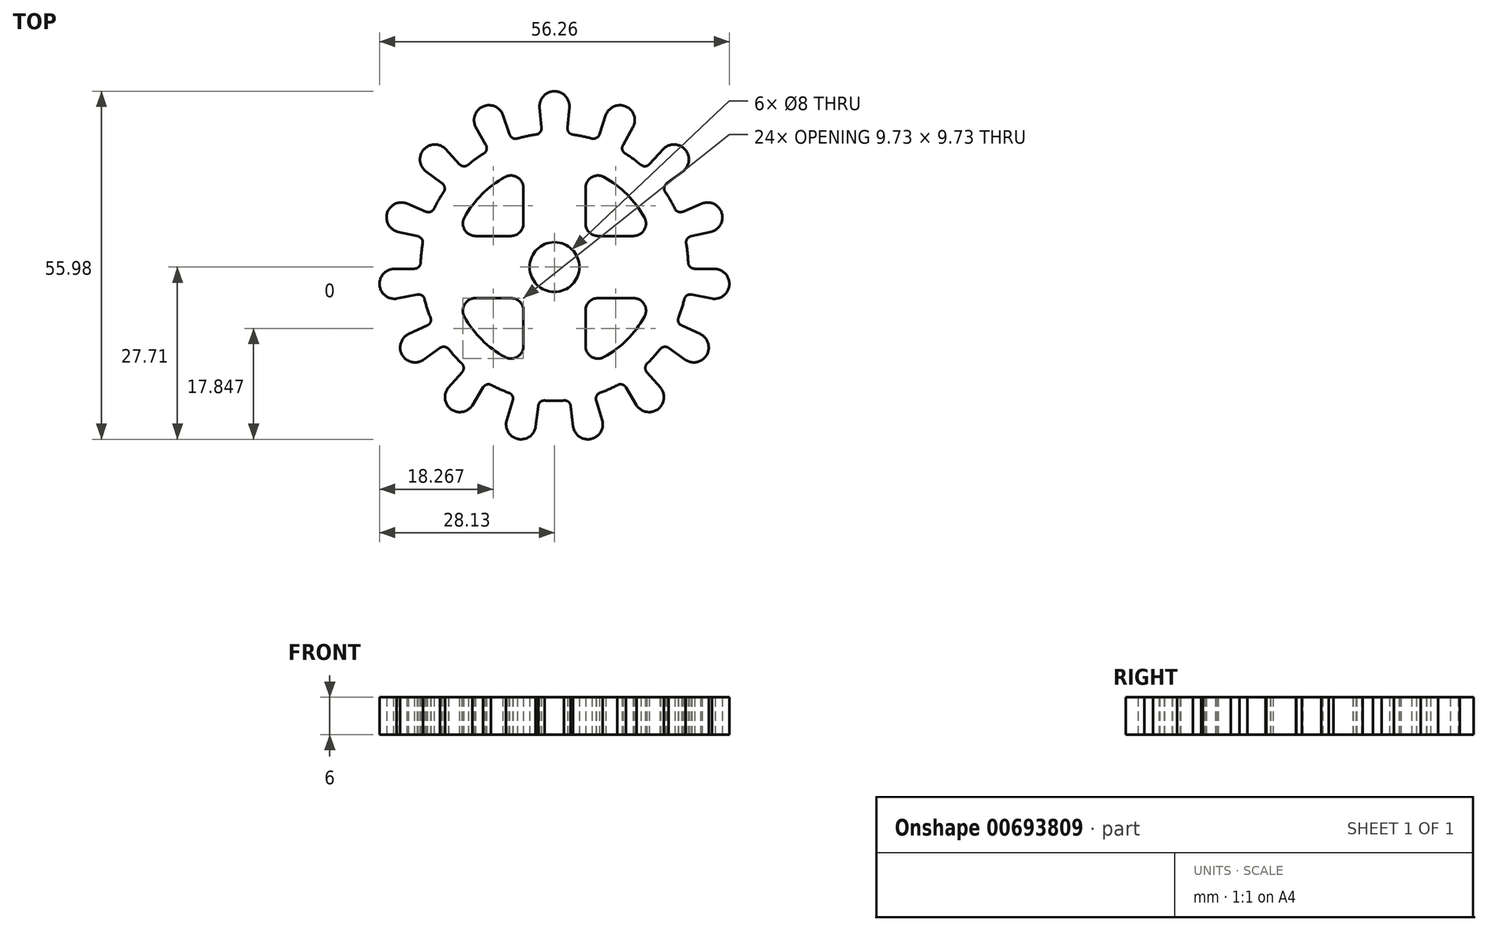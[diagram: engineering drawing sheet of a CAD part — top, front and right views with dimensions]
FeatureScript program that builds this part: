
annotation { "Feature Type Name" : "Feature", "Feature Type Description" : "" }
export const myFeature = defineFeature(function(context is Context, id is Id, definition is map)
    precondition{}
    {
        {
            var Q0;
            Q0=qCreatedBy(makeId("Top.planeOp"),FACE);
            var sketch = newSketch(context, id + "F0", { "sketchPlane" : qUnion([Q0])});
            skCircle(sketch, "E0", {"center": v(0, 0) * mm, "radius": 25.88 * mm, "construction": true});
            skArc(sketch, "E1", {"start": v(-2.4, 25.76) * mm, "mid": v(0, 28.28) * mm, "end": v(2.4, 25.76) * mm});
            skLineSegment(sketch, "E2.anchor1", {"start": v(0, 0) * mm, "end": v(0, 25.88) * mm, "construction": true});
            skLineSegment(sketch, "E3", {"start": v(2.4, 25.76) * mm, "end": v(2.09, 22.43) * mm});
            skLineSegment(sketch, "E4", {"start": v(8.29, 24.51) * mm, "end": v(7.22, 21.34) * mm});
            skArc(sketch, "E5", {"start": v(2.09, 22.43) * mm, "mid": v(2.3, 21.68) * mm, "end": v(2.99, 21.32) * mm});
            skArc(sketch, "E6", {"start": v(6.03, 20.66) * mm, "mid": v(6.75, 20.77) * mm, "end": v(7.22, 21.34) * mm});
            skArc(sketch, "E7", {"start": v(6.03, 20.66) * mm, "mid": v(4.52, 21.05) * mm, "end": v(2.99, 21.32) * mm});
            skLineSegment(sketch, "E8.1.0", {"start": v(12.67, 22.56) * mm, "end": v(11.03, 19.64) * mm});
            skArc(sketch, "E8.1.1", {"start": v(13.91, 16.43) * mm, "mid": v(12.69, 17.39) * mm, "end": v(11.4, 18.26) * mm});
            skArc(sketch, "E8.1.2", {"start": v(8.29, 24.51) * mm, "mid": v(11.5, 25.83) * mm, "end": v(12.67, 22.56) * mm});
            skLineSegment(sketch, "E8.1.3", {"start": v(17.54, 19.02) * mm, "end": v(15.27, 16.56) * mm});
            skArc(sketch, "E8.1.4", {"start": v(13.91, 16.43) * mm, "mid": v(14.62, 16.22) * mm, "end": v(15.27, 16.56) * mm});
            skArc(sketch, "E8.1.5", {"start": v(11.03, 19.64) * mm, "mid": v(10.92, 18.87) * mm, "end": v(11.4, 18.26) * mm});
            skLineSegment(sketch, "E8.2.0", {"start": v(20.75, 15.46) * mm, "end": v(18.06, 13.46) * mm});
            skArc(sketch, "E8.2.1", {"start": v(19.39, 9.35) * mm, "mid": v(18.66, 10.72) * mm, "end": v(17.84, 12.04) * mm});
            skArc(sketch, "E8.2.2", {"start": v(17.54, 19.02) * mm, "mid": v(21.01, 18.92) * mm, "end": v(20.75, 15.46) * mm});
            skLineSegment(sketch, "E8.2.3", {"start": v(23.76, 10.24) * mm, "end": v(20.69, 8.92) * mm});
            skArc(sketch, "E8.2.4", {"start": v(19.39, 9.35) * mm, "mid": v(19.95, 8.88) * mm, "end": v(20.69, 8.92) * mm});
            skArc(sketch, "E8.2.5", {"start": v(18.06, 13.46) * mm, "mid": v(17.65, 12.8) * mm, "end": v(17.84, 12.04) * mm});
            skLineSegment(sketch, "E8.3.0", {"start": v(25.24, 5.68) * mm, "end": v(21.98, 4.95) * mm});
            skArc(sketch, "E8.3.1", {"start": v(21.52, 0.65) * mm, "mid": v(21.41, 2.2) * mm, "end": v(21.2, 3.75) * mm});
            skArc(sketch, "E8.3.2", {"start": v(23.76, 10.24) * mm, "mid": v(26.9, 8.74) * mm, "end": v(25.24, 5.68) * mm});
            skLineSegment(sketch, "E8.3.3", {"start": v(25.87, -0.3) * mm, "end": v(22.52, -0.27) * mm});
            skArc(sketch, "E8.3.4", {"start": v(21.52, 0.65) * mm, "mid": v(21.84, 0) * mm, "end": v(22.52, -0.27) * mm});
            skArc(sketch, "E8.3.5", {"start": v(21.98, 4.95) * mm, "mid": v(21.33, 4.5) * mm, "end": v(21.2, 3.75) * mm});
            skLineSegment(sketch, "E8.4.0", {"start": v(25.37, -5.08) * mm, "end": v(22.09, -4.42) * mm});
            skArc(sketch, "E8.4.1", {"start": v(19.92, -8.15) * mm, "mid": v(20.46, -6.7) * mm, "end": v(20.89, -5.2) * mm});
            skArc(sketch, "E8.4.2", {"start": v(25.87, -0.3) * mm, "mid": v(28.12, -2.96) * mm, "end": v(25.37, -5.08) * mm});
            skLineSegment(sketch, "E8.4.3", {"start": v(23.51, -10.8) * mm, "end": v(20.47, -9.4) * mm});
            skArc(sketch, "E8.4.4", {"start": v(19.92, -8.15) * mm, "mid": v(19.95, -8.89) * mm, "end": v(20.47, -9.4) * mm});
            skArc(sketch, "E8.4.5", {"start": v(22.09, -4.42) * mm, "mid": v(21.32, -4.56) * mm, "end": v(20.89, -5.2) * mm});
            skLineSegment(sketch, "E8.5.0", {"start": v(21.11, -14.96) * mm, "end": v(18.38, -13.02) * mm});
            skArc(sketch, "E8.5.1", {"start": v(14.88, -15.55) * mm, "mid": v(15.97, -14.44) * mm, "end": v(16.97, -13.25) * mm});
            skArc(sketch, "E8.5.2", {"start": v(23.51, -10.8) * mm, "mid": v(24.49, -14.14) * mm, "end": v(21.11, -14.96) * mm});
            skLineSegment(sketch, "E8.5.3", {"start": v(17.08, -19.43) * mm, "end": v(14.87, -16.92) * mm});
            skArc(sketch, "E8.5.4", {"start": v(14.88, -15.55) * mm, "mid": v(14.6, -16.23) * mm, "end": v(14.87, -16.92) * mm});
            skArc(sketch, "E8.5.5", {"start": v(18.38, -13.02) * mm, "mid": v(17.63, -12.84) * mm, "end": v(16.97, -13.25) * mm});
            skLineSegment(sketch, "E8.6.0", {"start": v(13.2, -22.25) * mm, "end": v(11.5, -19.37) * mm});
            skArc(sketch, "E8.6.1", {"start": v(7.27, -20.26) * mm, "mid": v(8.71, -19.68) * mm, "end": v(10.11, -19) * mm});
            skArc(sketch, "E8.6.2", {"start": v(17.08, -19.43) * mm, "mid": v(16.62, -22.87) * mm, "end": v(13.2, -22.25) * mm});
            skLineSegment(sketch, "E8.6.3", {"start": v(7.7, -24.7) * mm, "end": v(6.7, -21.5) * mm});
            skArc(sketch, "E8.6.4", {"start": v(7.27, -20.26) * mm, "mid": v(6.74, -20.77) * mm, "end": v(6.7, -21.5) * mm});
            skArc(sketch, "E8.6.5", {"start": v(11.5, -19.37) * mm, "mid": v(10.88, -18.9) * mm, "end": v(10.11, -19) * mm});
            skLineSegment(sketch, "E8.7.0", {"start": v(3.01, -25.7) * mm, "end": v(2.62, -22.37) * mm});
            skArc(sketch, "E8.7.1", {"start": v(-1.6, -21.47) * mm, "mid": v(-0.04, -21.52) * mm, "end": v(1.5, -21.47) * mm});
            skArc(sketch, "E8.7.2", {"start": v(7.7, -24.7) * mm, "mid": v(5.88, -27.66) * mm, "end": v(3.01, -25.7) * mm});
            skLineSegment(sketch, "E8.7.3", {"start": v(-3.01, -25.7) * mm, "end": v(-2.62, -22.37) * mm});
            skArc(sketch, "E8.7.4", {"start": v(-1.6, -21.47) * mm, "mid": v(-2.29, -21.72) * mm, "end": v(-2.62, -22.37) * mm});
            skArc(sketch, "E8.7.5", {"start": v(2.62, -22.37) * mm, "mid": v(2.26, -21.69) * mm, "end": v(1.5, -21.47) * mm});
            skLineSegment(sketch, "E8.8.0", {"start": v(-7.7, -24.7) * mm, "end": v(-6.7, -21.5) * mm});
            skArc(sketch, "E8.8.1", {"start": v(-10.2, -18.96) * mm, "mid": v(-8.8, -19.65) * mm, "end": v(-7.35, -20.23) * mm});
            skArc(sketch, "E8.8.2", {"start": v(-3.01, -25.7) * mm, "mid": v(-5.88, -27.66) * mm, "end": v(-7.7, -24.7) * mm});
            skLineSegment(sketch, "E8.8.3", {"start": v(-13.2, -22.25) * mm, "end": v(-11.5, -19.37) * mm});
            skArc(sketch, "E8.8.4", {"start": v(-10.2, -18.96) * mm, "mid": v(-10.92, -18.9) * mm, "end": v(-11.5, -19.37) * mm});
            skArc(sketch, "E8.8.5", {"start": v(-6.7, -21.5) * mm, "mid": v(-6.76, -20.73) * mm, "end": v(-7.35, -20.23) * mm});
            skLineSegment(sketch, "E8.9.0", {"start": v(-17.08, -19.43) * mm, "end": v(-14.87, -16.92) * mm});
            skArc(sketch, "E8.9.1", {"start": v(-17.02, -13.18) * mm, "mid": v(-16.03, -14.37) * mm, "end": v(-14.95, -15.49) * mm});
            skArc(sketch, "E8.9.2", {"start": v(-13.2, -22.25) * mm, "mid": v(-16.62, -22.87) * mm, "end": v(-17.08, -19.43) * mm});
            skLineSegment(sketch, "E8.9.3", {"start": v(-21.11, -14.96) * mm, "end": v(-18.38, -13.02) * mm});
            skArc(sketch, "E8.9.4", {"start": v(-17.02, -13.18) * mm, "mid": v(-17.67, -12.83) * mm, "end": v(-18.38, -13.02) * mm});
            skArc(sketch, "E8.9.5", {"start": v(-14.87, -16.92) * mm, "mid": v(-14.6, -16.19) * mm, "end": v(-14.95, -15.49) * mm});
            skLineSegment(sketch, "E8.anchor1", {"start": v(0, 0) * mm, "end": v(-2.4, 25.76) * mm, "construction": true});
            skLineSegment(sketch, "E8.anchor2", {"start": v(0, 0) * mm, "end": v(-13.2, -22.25) * mm, "construction": true});
            skLineSegment(sketch, "E9.1.0", {"start": v(-25.37, -5.08) * mm, "end": v(-22.09, -4.42) * mm});
            skArc(sketch, "E9.1.1", {"start": v(-20.47, -9.4) * mm, "mid": v(-19.93, -8.85) * mm, "end": v(-19.95, -8.07) * mm});
            skArc(sketch, "E9.1.2", {"start": v(-20.9, -5.11) * mm, "mid": v(-21.36, -4.53) * mm, "end": v(-22.09, -4.42) * mm});
            skLineSegment(sketch, "E9.1.3", {"start": v(-23.51, -10.8) * mm, "end": v(-20.47, -9.4) * mm});
            skArc(sketch, "E9.1.4", {"start": v(-20.9, -5.11) * mm, "mid": v(-20.49, -6.6) * mm, "end": v(-19.95, -8.07) * mm});
            skArc(sketch, "E9.1.5", {"start": v(-21.11, -14.96) * mm, "mid": v(-24.49, -14.14) * mm, "end": v(-23.51, -10.8) * mm});
            skLineSegment(sketch, "E9.2.0", {"start": v(-25.24, 5.68) * mm, "end": v(-21.98, 4.95) * mm});
            skArc(sketch, "E9.2.1", {"start": v(-22.52, -0.27) * mm, "mid": v(-21.8, 0.02) * mm, "end": v(-21.51, 0.74) * mm});
            skArc(sketch, "E9.2.2", {"start": v(-21.18, 3.83) * mm, "mid": v(-21.36, 4.55) * mm, "end": v(-21.98, 4.95) * mm});
            skLineSegment(sketch, "E9.2.3", {"start": v(-25.87, -0.3) * mm, "end": v(-22.52, -0.27) * mm});
            skArc(sketch, "E9.2.4", {"start": v(-21.18, 3.83) * mm, "mid": v(-21.4, 2.3) * mm, "end": v(-21.51, 0.74) * mm});
            skArc(sketch, "E9.2.5", {"start": v(-25.37, -5.08) * mm, "mid": v(-28.12, -2.96) * mm, "end": v(-25.87, -0.3) * mm});
            skLineSegment(sketch, "E9.3.0", {"start": v(-20.75, 15.46) * mm, "end": v(-18.06, 13.46) * mm});
            skArc(sketch, "E9.3.1", {"start": v(-20.69, 8.92) * mm, "mid": v(-19.9, 8.9) * mm, "end": v(-19.35, 9.43) * mm});
            skArc(sketch, "E9.3.2", {"start": v(-17.8, 12.12) * mm, "mid": v(-17.66, 12.84) * mm, "end": v(-18.06, 13.46) * mm});
            skLineSegment(sketch, "E9.3.3", {"start": v(-23.76, 10.24) * mm, "end": v(-20.69, 8.92) * mm});
            skArc(sketch, "E9.3.4", {"start": v(-17.8, 12.12) * mm, "mid": v(-18.62, 10.8) * mm, "end": v(-19.35, 9.43) * mm});
            skArc(sketch, "E9.3.5", {"start": v(-25.24, 5.68) * mm, "mid": v(-26.9, 8.74) * mm, "end": v(-23.76, 10.24) * mm});
            skLineSegment(sketch, "E9.4.0", {"start": v(-12.67, 22.56) * mm, "end": v(-11.03, 19.64) * mm});
            skArc(sketch, "E9.4.1", {"start": v(-15.27, 16.56) * mm, "mid": v(-14.57, 16.22) * mm, "end": v(-13.84, 16.48) * mm});
            skArc(sketch, "E9.4.2", {"start": v(-11.32, 18.3) * mm, "mid": v(-10.91, 18.91) * mm, "end": v(-11.03, 19.64) * mm});
            skLineSegment(sketch, "E9.4.3", {"start": v(-17.54, 19.02) * mm, "end": v(-15.27, 16.56) * mm});
            skArc(sketch, "E9.4.4", {"start": v(-11.32, 18.3) * mm, "mid": v(-12.62, 17.44) * mm, "end": v(-13.84, 16.48) * mm});
            skArc(sketch, "E9.4.5", {"start": v(-20.75, 15.46) * mm, "mid": v(-21.01, 18.92) * mm, "end": v(-17.54, 19.02) * mm});
            skLineSegment(sketch, "E9.5.0", {"start": v(-2.4, 25.76) * mm, "end": v(-2.09, 22.43) * mm});
            skArc(sketch, "E9.5.1", {"start": v(-7.22, 21.34) * mm, "mid": v(-6.71, 20.75) * mm, "end": v(-5.94, 20.69) * mm});
            skArc(sketch, "E9.5.2", {"start": v(-2.9, 21.33) * mm, "mid": v(-2.28, 21.72) * mm, "end": v(-2.09, 22.43) * mm});
            skLineSegment(sketch, "E9.5.3", {"start": v(-8.29, 24.51) * mm, "end": v(-7.22, 21.34) * mm});
            skArc(sketch, "E9.5.4", {"start": v(-2.9, 21.33) * mm, "mid": v(-4.43, 21.06) * mm, "end": v(-5.94, 20.69) * mm});
            skArc(sketch, "E9.5.5", {"start": v(-12.67, 22.56) * mm, "mid": v(-11.5, 25.83) * mm, "end": v(-8.29, 24.51) * mm});
            skLineSegment(sketch, "E9.anchor1", {"start": v(0, 0) * mm, "end": v(-17.08, -19.43) * mm, "construction": true});
            skLineSegment(sketch, "E9.anchor2", {"start": v(0, 0) * mm, "end": v(-8.29, 24.51) * mm, "construction": true});
            skCircle(sketch, "E10", {"center": v(0, 0) * mm, "radius": 4 * mm});
            skLineSegment(sketch, "E11", {"start": v(12.73, 5) * mm, "end": v(7, 5) * mm});
            skLineSegment(sketch, "E12", {"start": v(5, 7) * mm, "end": v(5, 12.73) * mm});
            skArc(sketch, "E13.filletArc", {"start": v(5, 7) * mm, "mid": v(5.59, 5.59) * mm, "end": v(7, 5) * mm});
            skArc(sketch, "E14", {"start": v(7.96, 14.48) * mm, "mid": v(11.68, 11.68) * mm, "end": v(14.48, 7.96) * mm});
            skArc(sketch, "E15.filletArc", {"start": v(7.96, 14.48) * mm, "mid": v(5.98, 14.45) * mm, "end": v(5, 12.73) * mm});
            skArc(sketch, "E16.filletArc", {"start": v(12.73, 5) * mm, "mid": v(14.45, 5.98) * mm, "end": v(14.48, 7.96) * mm});
            skLineSegment(sketch, "E17.1.0", {"start": v(-5, 12.73) * mm, "end": v(-5, 7) * mm});
            skArc(sketch, "E17.1.1", {"start": v(-5, 12.73) * mm, "mid": v(-5.98, 14.45) * mm, "end": v(-7.96, 14.48) * mm});
            skArc(sketch, "E17.1.2", {"start": v(-14.48, 7.96) * mm, "mid": v(-11.68, 11.68) * mm, "end": v(-7.96, 14.48) * mm});
            skArc(sketch, "E17.1.3", {"start": v(-14.48, 7.96) * mm, "mid": v(-14.45, 5.98) * mm, "end": v(-12.73, 5) * mm});
            skLineSegment(sketch, "E17.1.4", {"start": v(-7, 5) * mm, "end": v(-12.73, 5) * mm});
            skArc(sketch, "E17.1.5", {"start": v(-7, 5) * mm, "mid": v(-5.59, 5.59) * mm, "end": v(-5, 7) * mm});
            skLineSegment(sketch, "E17.2.0", {"start": v(-12.73, -5) * mm, "end": v(-7, -5) * mm});
            skArc(sketch, "E17.2.1", {"start": v(-12.73, -5) * mm, "mid": v(-14.45, -5.98) * mm, "end": v(-14.48, -7.96) * mm});
            skArc(sketch, "E17.2.2", {"start": v(-7.96, -14.48) * mm, "mid": v(-11.68, -11.68) * mm, "end": v(-14.48, -7.96) * mm});
            skArc(sketch, "E17.2.3", {"start": v(-7.96, -14.48) * mm, "mid": v(-5.98, -14.45) * mm, "end": v(-5, -12.73) * mm});
            skLineSegment(sketch, "E17.2.4", {"start": v(-5, -7) * mm, "end": v(-5, -12.73) * mm});
            skArc(sketch, "E17.2.5", {"start": v(-5, -7) * mm, "mid": v(-5.59, -5.59) * mm, "end": v(-7, -5) * mm});
            skLineSegment(sketch, "E17.3.0", {"start": v(5, -12.73) * mm, "end": v(5, -7) * mm});
            skArc(sketch, "E17.3.1", {"start": v(5, -12.73) * mm, "mid": v(5.98, -14.45) * mm, "end": v(7.96, -14.48) * mm});
            skArc(sketch, "E17.3.2", {"start": v(14.48, -7.96) * mm, "mid": v(11.68, -11.68) * mm, "end": v(7.96, -14.48) * mm});
            skArc(sketch, "E17.3.3", {"start": v(14.48, -7.96) * mm, "mid": v(14.45, -5.98) * mm, "end": v(12.73, -5) * mm});
            skLineSegment(sketch, "E17.3.4", {"start": v(7, -5) * mm, "end": v(12.73, -5) * mm});
            skArc(sketch, "E17.3.5", {"start": v(7, -5) * mm, "mid": v(5.59, -5.59) * mm, "end": v(5, -7) * mm});
            skSolve(sketch);
        }
        {
            var Q0;
            Q0 = qSketchRegion(id + "F0", true);
            extrude(context, id + "F1", {"entities" : qUnion([Q0]), "depth" : 6 * mm, "offsetDistance" : 25 * mm});
        }
    });
